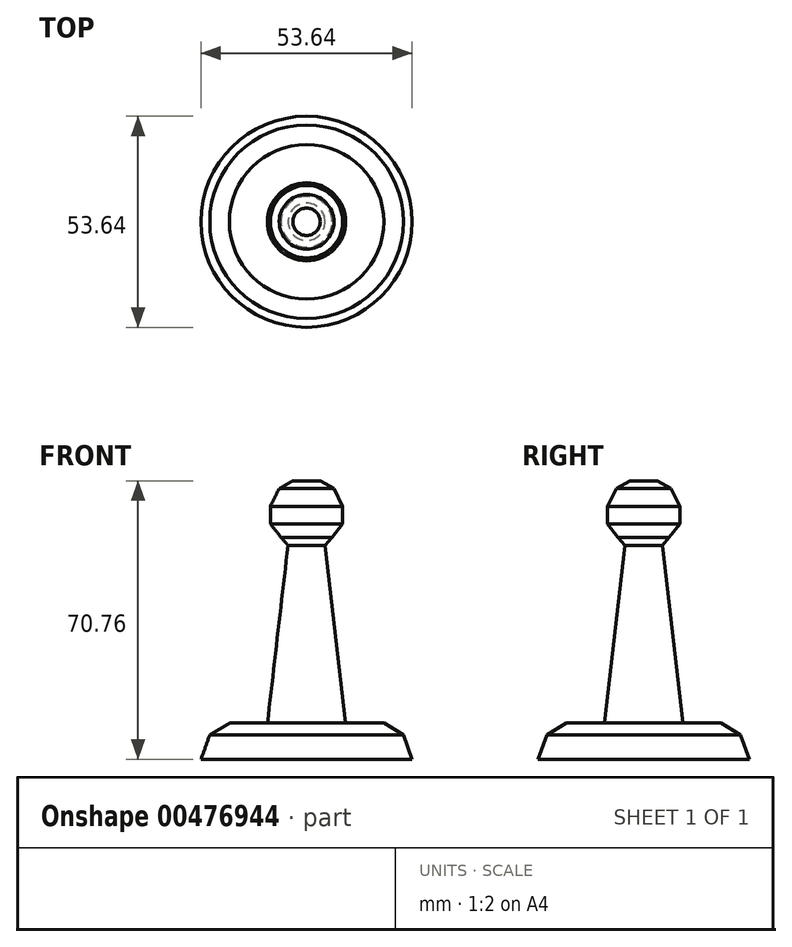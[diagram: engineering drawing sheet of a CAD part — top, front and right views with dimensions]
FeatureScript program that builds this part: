
annotation { "Feature Type Name" : "Feature", "Feature Type Description" : "" }
export const myFeature = defineFeature(function(context is Context, id is Id, definition is map)
    precondition{}
    {
        {
            var Q0;
            Q0=qCreatedBy(makeId("Front.planeOp"),FACE);
            var sketch = newSketch(context, id + "F0", { "sketchPlane" : qUnion([Q0])});
            skLineSegment(sketch, "E0", {"start": v(0, 41.34) * mm, "end": v(-3.48, 41.34) * mm});
            skLineSegment(sketch, "E1", {"start": v(-3.48, 41.34) * mm, "end": v(-6.96, 39.35) * mm});
            skLineSegment(sketch, "E2", {"start": v(-6.96, 39.35) * mm, "end": v(-9.2, 34.88) * mm});
            skLineSegment(sketch, "E3", {"start": v(-9.2, 34.88) * mm, "end": v(-9.2, 30.42) * mm});
            skLineSegment(sketch, "E4", {"start": v(-9.2, 30.42) * mm, "end": v(-6.46, 26.94) * mm});
            skLineSegment(sketch, "E5", {"start": v(-6.46, 26.94) * mm, "end": v(-4.72, 24.95) * mm});
            skLineSegment(sketch, "E6", {"start": v(-4.72, 24.95) * mm, "end": v(-9.94, -20.23) * mm});
            skLineSegment(sketch, "E7", {"start": v(-9.94, -20.23) * mm, "end": v(-19.62, -20.23) * mm});
            skLineSegment(sketch, "E8", {"start": v(-19.62, -20.23) * mm, "end": v(-24.58, -23.21) * mm});
            skLineSegment(sketch, "E9", {"start": v(-24.58, -23.21) * mm, "end": v(-26.82, -29.42) * mm});
            skLineSegment(sketch, "E10", {"start": v(-26.82, -29.42) * mm, "end": v(0, -29.42) * mm});
            skLineSegment(sketch, "E11", {"start": v(0, -29.42) * mm, "end": v(0, 41.34) * mm});
            skSolve(sketch);
        }
        {
            var Q0;
            Q0=makeQuery(id+"F0.imprint","IMPRINT",FACE,{"disambiguationData":[TD([[makeQuery(id+"F0.imprint","IMPRINT",EDGE,{"derivedFrom":sQuery(id+"F0.wireOp",EDGE,"E0")}),1.0]])]});
            var Q1;
            Q1=sQuery(id+"F0.wireOp",EDGE,"E11");
            revolve(context, id + "F1", {"entities" : qUnion([Q0]), "axis" : qUnion([Q1]), "revolveType" : RevolveType.FULL});
        }
    });
